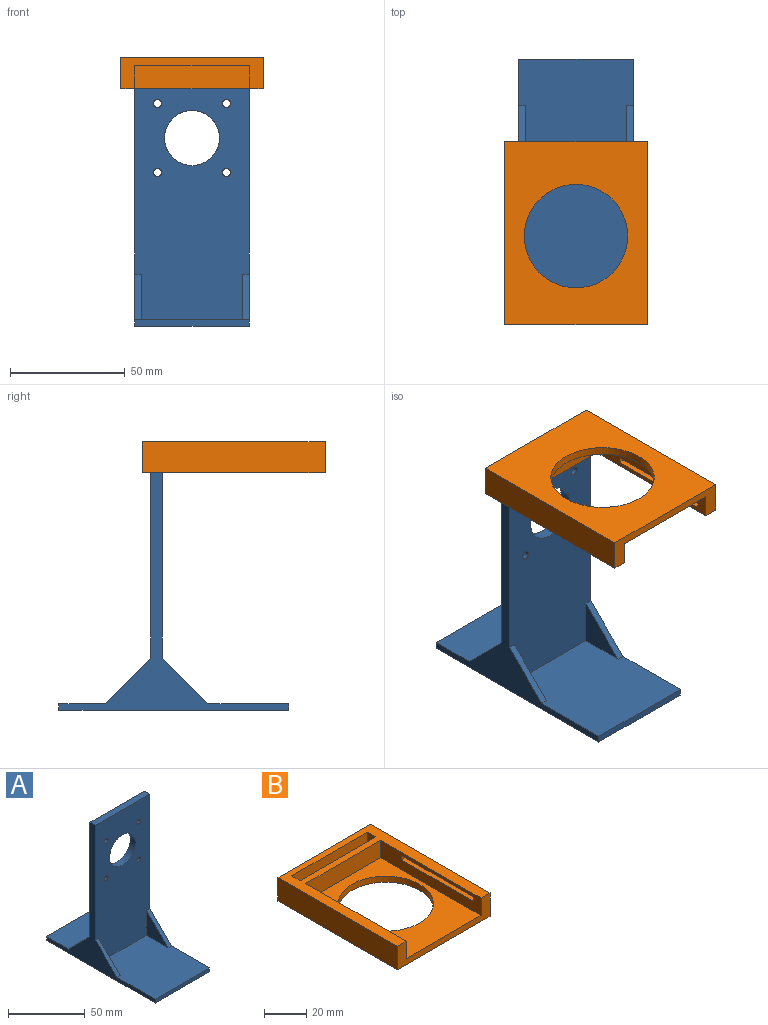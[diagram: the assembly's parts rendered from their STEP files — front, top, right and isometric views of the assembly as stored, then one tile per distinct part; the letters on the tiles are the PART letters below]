
ASSEMBLY  parts=2 mates=1
PART A: 23 faces, bbox 50x100x114 mm
  f0: plane 111x50mm, normal (0,-1,0), area 4938.1mm2, adj f3,f5,f6,f9,f10,f11,f12,f13
  f1: plane 50x40mm, normal (0,0,1), area 1881.2mm2, adj f3,f4,f5,f8,f16,f17,f18,f19
  f2: plane 50x3mm, normal (0,-1,0), area 150mm2, adj f3,f5,f6,f7
  f3: plane 114x100mm, normal (1,0,0), area 1247mm2, adj f0,f1,f2,f4,f6,f7,f8,f14
  f4: plane 50x3mm, normal (0,1,0), area 150mm2, adj f1,f3,f5,f7
  f5: plane 114x100mm, normal (-1,0,0), area 1247mm2, adj f0,f1,f2,f4,f6,f7,f8,f18
  f6: plane 55x50mm, normal (0,0,1), area 2631.2mm2, adj f0,f2,f3,f5,f14,f15,f20,f21
  f7: plane 100x50mm, normal (0,0,-1), area 5000mm2, adj f2,f3,f4,f5
  f8: plane 111x50mm, normal (0,1,0), area 4938.1mm2, adj f1,f3,f5,f9,f10,f11,f12,f13
  f9: cylinder r=1.8mm len=5mm, axis (0,-1,0), area 56.5mm2, adj f0,f8
  f10: cylinder r=1.8mm len=5mm, axis (0,-1,0), area 56.5mm2, adj f0,f8
  f11: cylinder r=1.8mm len=5mm, axis (0,-1,0), area 56.5mm2, adj f0,f8
  f12: cylinder r=1.8mm len=5mm, axis (0,-1,0), area 56.5mm2, adj f0,f8
  f13: cylinder r=12mm len=24mm, axis (0,-1,0), area 377mm2, adj f0,f8
  f14: plane 19.8x19.8mm, normal (0,-0.71,0.71), area 84mm2, adj f0,f3,f6,f15
  f15: plane 19.8x19.8mm, normal (-1,0,0), area 196mm2, adj f0,f6,f14
  f16: plane 19.8x19.8mm, normal (0,0.71,0.71), area 84mm2, adj f1,f3,f8,f17
  f17: plane 19.8x19.8mm, normal (-1,0,0), area 196mm2, adj f1,f8,f16
  f18: plane 19.8x19.8mm, normal (0,0.71,0.71), area 84mm2, adj f1,f5,f8,f19
  f19: plane 19.8x19.8mm, normal (1,0,0), area 196mm2, adj f1,f8,f18
  f20: plane 19.8x19.8mm, normal (0,-0.71,0.71), area 84mm2, adj f0,f5,f6,f21
  f21: plane 19.8x19.8mm, normal (1,0,0), area 196mm2, adj f0,f6,f20
  f22: plane 50x5mm, normal (0,0,1), area 250mm2, adj f0,f3,f5,f8
PART B: 26 faces, bbox 62x79.6x13.5 mm
  f0: plane 50x10mm, normal (0,-1,0), area 500mm2, adj f3,f4,f15,f20
  f1: plane 3x2.5mm, normal (0,1,0), area 7.5mm2, adj f3,f5,f23,f25
  f2: plane 3x2.5mm, normal (0,1,0), area 7.5mm2, adj f4,f17,f22,f24
  f3: plane 67x10mm, normal (-1,0,0), area 550mm2, adj f0,f1,f15,f19,f20,f21,f23,f25
  f4: plane 67x10mm, normal (1,0,0), area 550mm2, adj f0,f2,f15,f18,f20,f21,f22,f24
  f5: plane 48x2.5mm, normal (-1,0,0), area 120mm2, adj f1,f19,f23,f25
  f6: cylinder r=22.5mm len=45mm, axis (0,0,1), area 494.8mm2, adj f9,f20
  f7: plane 79.6x13.5mm, normal (1,0,0), area 1074.6mm2, adj f9,f10,f15,f21
  f8: plane 79.6x13.5mm, normal (-1,0,0), area 1074.6mm2, adj f9,f10,f15,f21
  f9: plane 79.6x62mm, normal (0,0,-1), area 3344.8mm2, adj f6,f7,f8,f10,f21
  f10: plane 62x13.5mm, normal (0,1,0), area 837mm2, adj f7,f8,f9,f15
  f11: plane 10.5x5.6mm, normal (1,0,0), area 58.8mm2, adj f12,f14,f15,f16
  f12: plane 50.6x10.5mm, normal (0,-1,0), area 531.3mm2, adj f11,f13,f15,f16
  f13: plane 10.5x5.6mm, normal (-1,0,0), area 58.8mm2, adj f12,f14,f15,f16
  f14: plane 50.6x10.5mm, normal (0,1,0), area 531.3mm2, adj f11,f13,f15,f16
  f15: plane 79.6x62mm, normal (0,0,1), area 1301.8mm2, adj f0,f3,f4,f7,f8,f10,f11,f12
  f16: plane 50.6x5.6mm, normal (0,0,1), area 283.4mm2, adj f11,f12,f13,f14
  f17: plane 48x2.5mm, normal (1,0,0), area 120mm2, adj f2,f18,f22,f24
  f18: plane 3x2.5mm, normal (0,-1,0), area 7.5mm2, adj f4,f17,f22,f24
  f19: plane 3x2.5mm, normal (0,-1,0), area 7.5mm2, adj f3,f5,f23,f25
  f20: plane 67x50mm, normal (0,0,1), area 1759.6mm2, adj f0,f3,f4,f6,f21
  f21: plane 62x13.5mm, normal (0,-1,0), area 337mm2, adj f3,f4,f7,f8,f9,f15,f20
  f22: plane 48x3mm, normal (0,0,-1), area 144mm2, adj f2,f4,f17,f18
  f23: plane 48x3mm, normal (0,0,-1), area 144mm2, adj f1,f3,f5,f19
  f24: plane 48x3mm, normal (0,0,1), area 144mm2, adj f2,f4,f17,f18
  f25: plane 48x3mm, normal (0,0,1), area 144mm2, adj f1,f3,f5,f19
PLACE A t=(-7.55,4.38,-43.9)mm
PLACE B rot(axis=(0,1,0),180deg) t=(-7.55,-16.82,73.1)mm
MATE fastened B.f16 <-> A.f22  axis (0,0,-1) through (-7.55,11.88,70.1)mm
